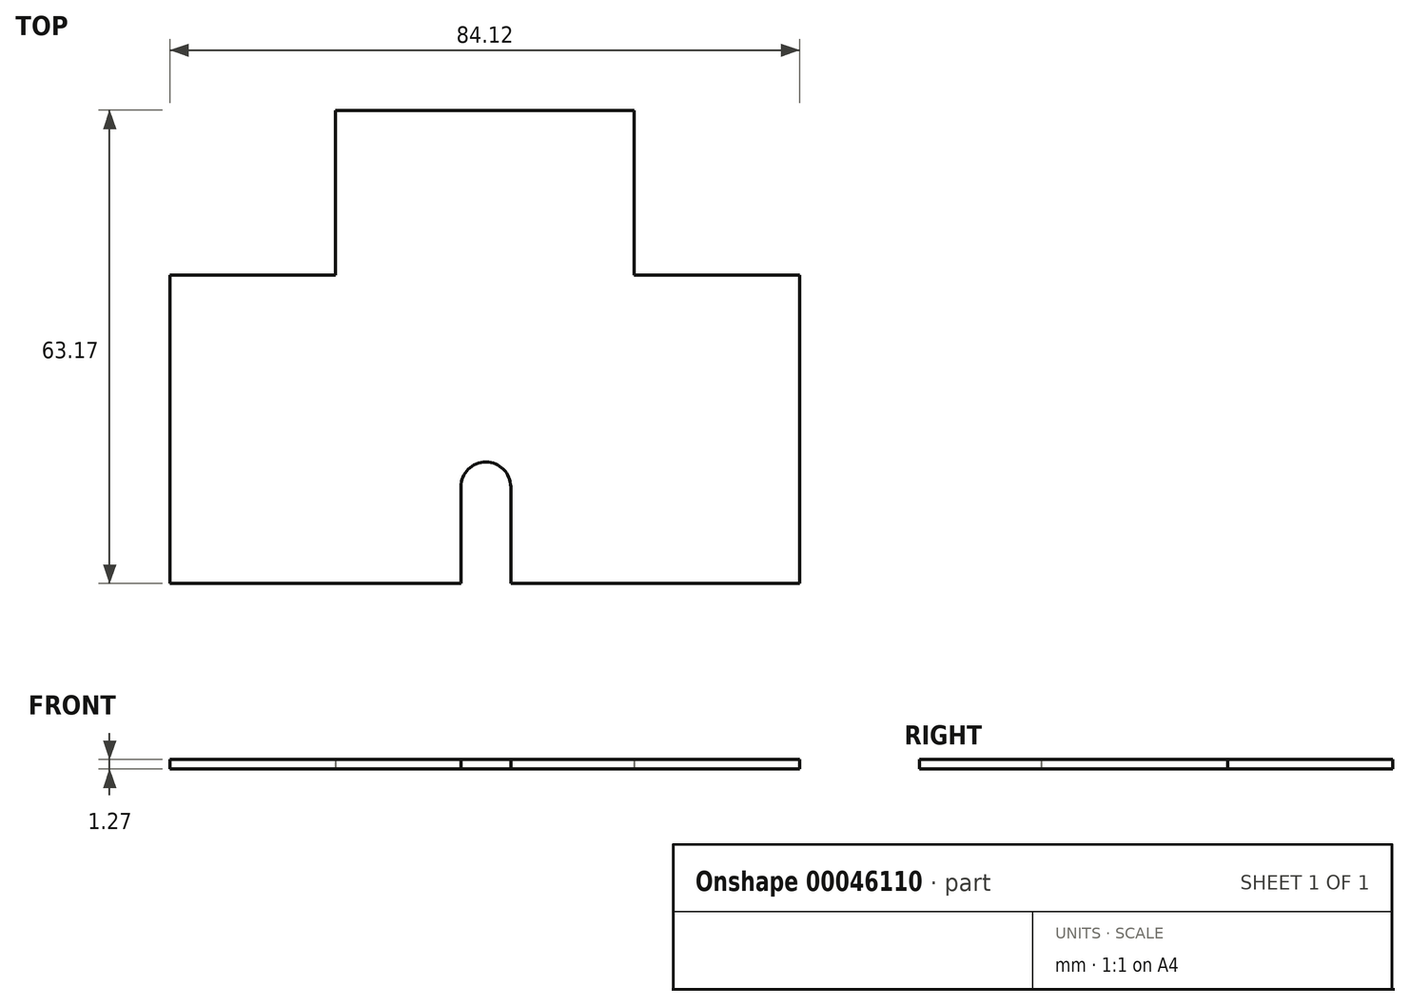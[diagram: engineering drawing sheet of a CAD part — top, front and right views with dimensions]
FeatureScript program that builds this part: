
annotation { "Feature Type Name" : "Feature", "Feature Type Description" : "" }
export const myFeature = defineFeature(function(context is Context, id is Id, definition is map)
    precondition{}
    {
        {
            var Q0;
            Q0=qCreatedBy(makeId("Top.planeOp"),FACE);
            var sketch = newSketch(context, id + "F0", { "sketchPlane" : qUnion([Q0])});
            skLineSegment(sketch, "E0.MirrorCS", {"start": v(-42.2, -22.23) * mm, "end": v(-3.32, -22.23) * mm});
            skLineSegment(sketch, "E1", {"start": v(-42.2, 18.93) * mm, "end": v(-20.1, 18.93) * mm});
            skLineSegment(sketch, "E2", {"start": v(-20.1, 18.93) * mm, "end": v(-20.1, 40.94) * mm});
            skLineSegment(sketch, "E3.MirrorCS", {"start": v(41.91, 18.93) * mm, "end": v(19.8, 18.93) * mm});
            skLineSegment(sketch, "E4", {"start": v(-3.32, -9.32) * mm, "end": v(-3.32, -22.23) * mm});
            skLineSegment(sketch, "E5.MirrorCS", {"start": v(3.32, -9.32) * mm, "end": v(3.32, -22.23) * mm});
            skArc(sketch, "E6", {"start": v(3.32, -9.32) * mm, "mid": v(0, -6) * mm, "end": v(-3.32, -9.32) * mm});
            skLineSegment(sketch, "E7.trimOffspring", {"start": v(3.32, -22.23) * mm, "end": v(41.91, -22.23) * mm});
            skLineSegment(sketch, "E8", {"start": v(19.8, 18.93) * mm, "end": v(19.8, 40.94) * mm});
            skLineSegment(sketch, "E9", {"start": v(19.8, 40.94) * mm, "end": v(-20.1, 40.94) * mm});
            skPoint(sketch, "E10.endSnap0", {"position": v(41.91, 0) * mm});
            skLineSegment(sketch, "E11", {"start": v(-42.2, -22.23) * mm, "end": v(-42.2, 18.93) * mm});
            skLineSegment(sketch, "E12", {"start": v(41.91, 18.93) * mm, "end": v(41.91, -22.23) * mm});
            skSolve(sketch);
        }
        {
            var Q0;
            Q0 = qSketchRegion(id + "F0", true);
            extrude(context, id + "F1", {"entities" : qUnion([Q0]), "depth" : 1.27 * mm});
        }
    });
